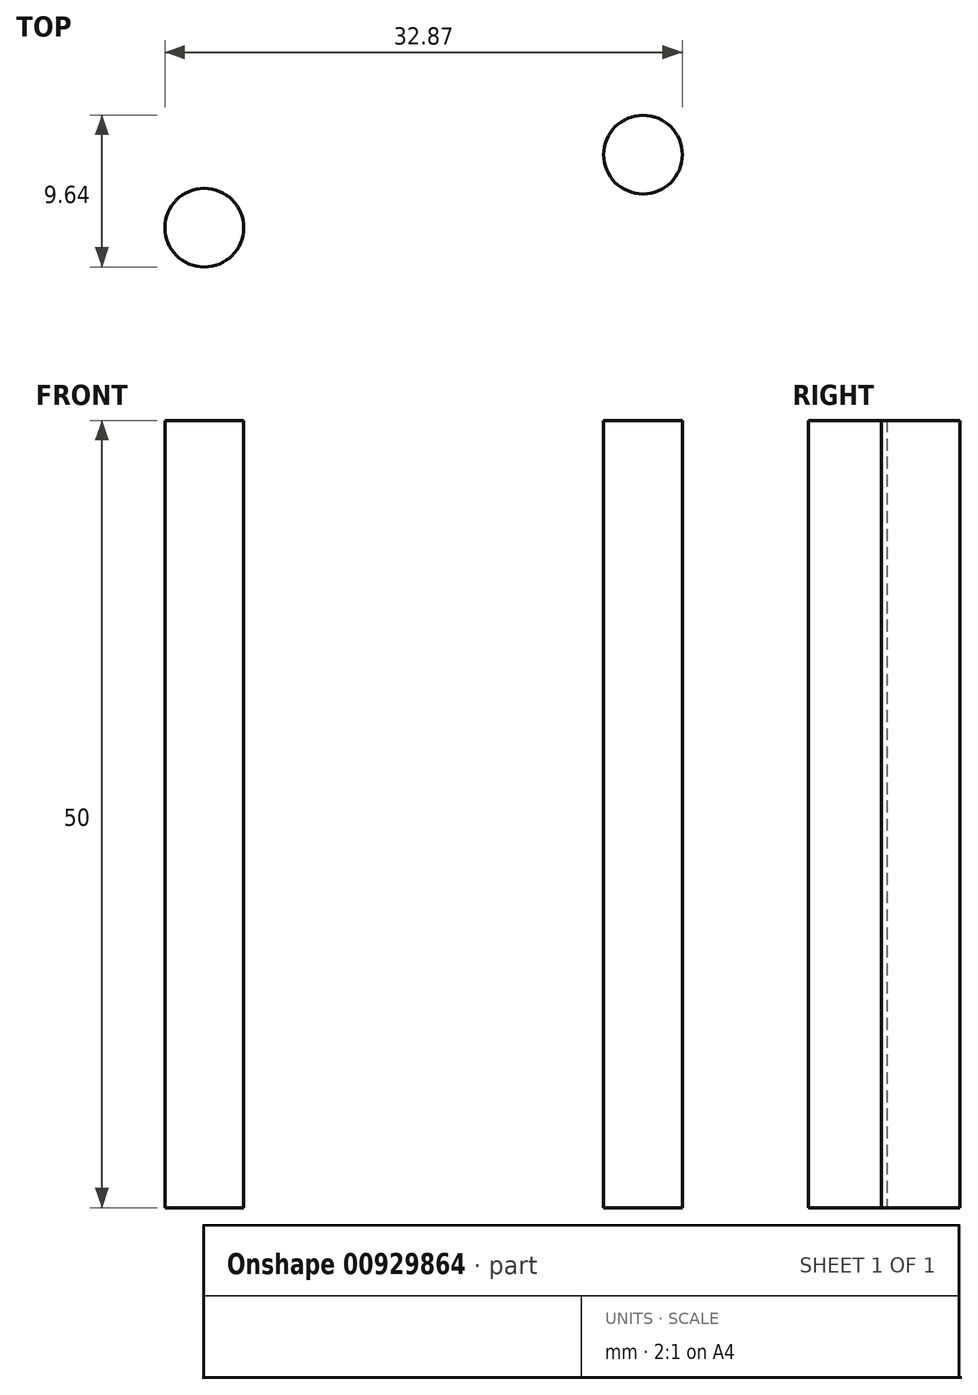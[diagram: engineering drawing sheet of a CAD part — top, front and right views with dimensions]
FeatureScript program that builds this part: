
annotation { "Feature Type Name" : "Feature", "Feature Type Description" : "" }
export const myFeature = defineFeature(function(context is Context, id is Id, definition is map)
    precondition{}
    {
        {
            var Q0;
            Q0=qCreatedBy(makeId("Top.planeOp"),FACE);
            var sketch = newSketch(context, id + "F0", { "sketchPlane" : qUnion([Q0])});
            skCircle(sketch, "E0", {"center": v(-41.17, 13.83) * mm, "radius": 2.5 * mm});
            skCircle(sketch, "E1", {"center": v(-13.3, 18.47) * mm, "radius": 2.5 * mm});
            skSolve(sketch);
        }
        {
            var Q0;
            Q0=makeQuery(id+"F0.imprint","IMPRINT",FACE,{"disambiguationData":[TD([[makeQuery(id+"F0.imprint","IMPRINT",EDGE,{"derivedFrom":sQuery(id+"F0.wireOp",EDGE,"E0")}),1.0]])]});
            var Q1;
            Q1=makeQuery(id+"F0.imprint","IMPRINT",FACE,{"disambiguationData":[TD([[makeQuery(id+"F0.imprint","IMPRINT",EDGE,{"derivedFrom":sQuery(id+"F0.wireOp",EDGE,"E1")}),1.0]])]});
            extrude(context, id + "F1", {"entities" : qUnion([Q0, Q1]), "depth" : 50 * mm, "offsetDistance" : 25.4 * mm});
        }
    });
